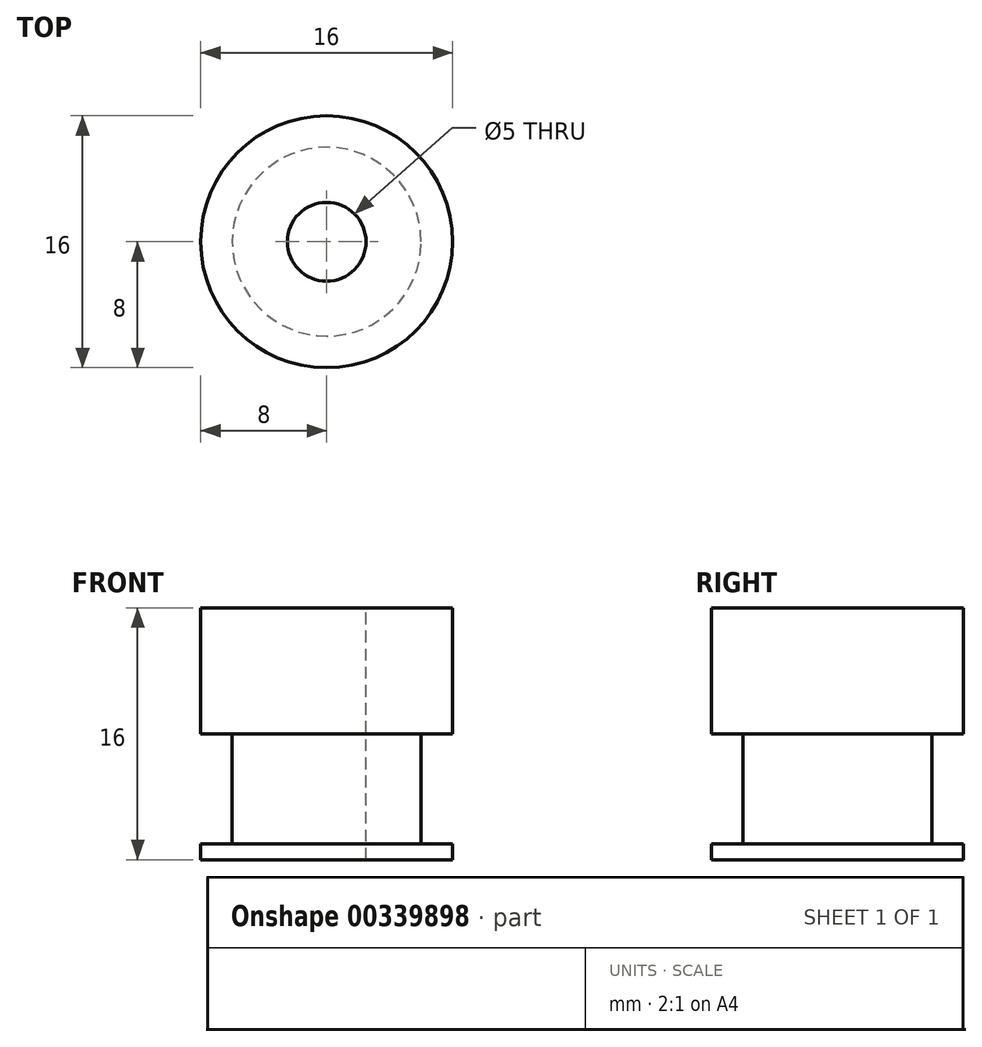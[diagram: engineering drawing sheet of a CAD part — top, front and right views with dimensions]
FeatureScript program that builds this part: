
annotation { "Feature Type Name" : "Feature", "Feature Type Description" : "" }
export const myFeature = defineFeature(function(context is Context, id is Id, definition is map)
    precondition{}
    {
        {
            var Q0;
            Q0=qCreatedBy(makeId("Top.planeOp"),FACE);
            var sketch = newSketch(context, id + "F0", { "sketchPlane" : qUnion([Q0])});
            skCircle(sketch, "E0", {"center": v(0, 0) * mm, "radius": 8 * mm});
            skCircle(sketch, "E1", {"center": v(0, 0) * mm, "radius": 6 * mm});
            skSolve(sketch);
        }
        {
            var Q0;
            Q0=makeQuery(id+"F0.imprint","IMPRINT",FACE,{"disambiguationData":[TD([[makeQuery(id+"F0.imprint","IMPRINT",EDGE,{"derivedFrom":sQuery(id+"F0.wireOp",EDGE,"E1")}),1.0]])]});
            var Q1;
            Q1=makeQuery(id+"F0.imprint","IMPRINT",FACE,{"disambiguationData":[TD([[makeQuery(id+"F0.imprint","IMPRINT",EDGE,{"derivedFrom":sQuery(id+"F0.wireOp",EDGE,"E0")}),1.0]])]});
            extrude(context, id + "F1", {"entities" : qUnion([Q0, Q1]), "depth" : 8 * mm});
        }
        {
            var Q0;
            Q0=makeQuery(id+"F0.imprint","IMPRINT",FACE,{"disambiguationData":[TD([[makeQuery(id+"F0.imprint","IMPRINT",EDGE,{"derivedFrom":sQuery(id+"F0.wireOp",EDGE,"E1")}),1.0]])]});
            extrude(context, id + "F2", {"entities" : qUnion([Q0]), "operationType" : NewBodyOperationType.ADD, "oppositeDirection" : true, "depth" : 7 * mm});
        }
        {
            var Q0;
            Q0=makeQuery(id+"F2.opExtrude","CAP_FACE",FACE,{"disambiguationData":[OSD([sQuery(id+"F0.wireOp",EDGE,"E1")])],"isStart":false});
            var sketch = newSketch(context, id + "F3", { "sketchPlane" : qUnion([Q0])});
            skCircle(sketch, "E2", {"center": v(0, 0) * mm, "radius": 8 * mm});
            skCircle(sketch, "E3", {"center": v(0, 0) * mm, "radius": 2.5 * mm});
            skSolve(sketch);
        }
        {
            var Q0;
            Q0=makeQuery(id+"F3.imprint","IMPRINT",FACE,{"disambiguationData":[TD([[makeQuery(id+"F3.imprint","IMPRINT",EDGE,{"derivedFrom":makeQuery(id+"F2.opExtrude","CAP_EDGE",EDGE,{"disambiguationData":[OSD([sQuery(id+"F0.wireOp",EDGE,"E1")])],"isStart":false})}),-1.0]])]});
            var Q1;
            Q1=makeQuery(id+"F3.imprint","IMPRINT",FACE,{"disambiguationData":[TD([[makeQuery(id+"F3.imprint","IMPRINT",EDGE,{"derivedFrom":sQuery(id+"F3.wireOp",EDGE,"E2")}),1.0]])]});
            extrude(context, id + "F4", {"entities" : qUnion([Q0, Q1]), "operationType" : NewBodyOperationType.ADD, "depth" : 1 * mm});
        }
        {
            var Q0;
            Q0=makeQuery(id+"F3.imprint","IMPRINT",FACE,{"disambiguationData":[TD([[makeQuery(id+"F3.imprint","IMPRINT",EDGE,{"derivedFrom":sQuery(id+"F3.wireOp",EDGE,"E3")}),1.0]])]});
            var Q1;
            Q1 = qSketchRegion(id + "FLtDxuVyBBL1WI3_1", true);
            extrude(context, id + "F5", {"entities" : qUnion([Q0, Q1]), "operationType" : NewBodyOperationType.REMOVE, "endBound" : BoundingType.THROUGH_ALL, "oppositeDirection" : true, "depth" : 25 * mm});
        }
    });
